# Revit family: QF_BOURGEAT_Transtherm_Four_sur_pietement_bas_5GN1_2
name_source: partatom
category: Equipement spécialisé
revit_build: Autodesk Revit 2015 (Build: 20140606_1530(x64)
units: mm (PartAtom-declared; Revit-internal decimal feet)

## types (2) — shared parameters
Certification = NF alimentaire
Charge max = 10.00 kg
Consommation énergétique = 1.5Kwh/h
Fabricant = BOURGEAT
Fréquence = 50 Hz
Hauteur hors tout = 810 mm
Indice de protection = IP25
Intensité nominale = 10 A
Longueur hors tout = 418 mm  [stored 1.37139 ft]
Nature isolant = Laine_de_roche(60mm)
Phase = 3
Poids net à vide = 28.00 kg
Profondeur hors tout = 577 mm  [stored 1.89304 ft]
Puissance électrique  = 2200 W
Spécification du Fabricant = TRANS'THERM
Tension = 230 V
URL catalogue = http://www.bourgeat.fr

## type names (no varying parameters)
- 892004 + 895104
- 892004 + 897500 + 895104

note: column(s) folded — value = type name in every type: Modèle, Type_de_modele

note: [stored X ft] marks values corroborated as IEEE doubles in the binary element streams (Revit-internal decimal feet)
